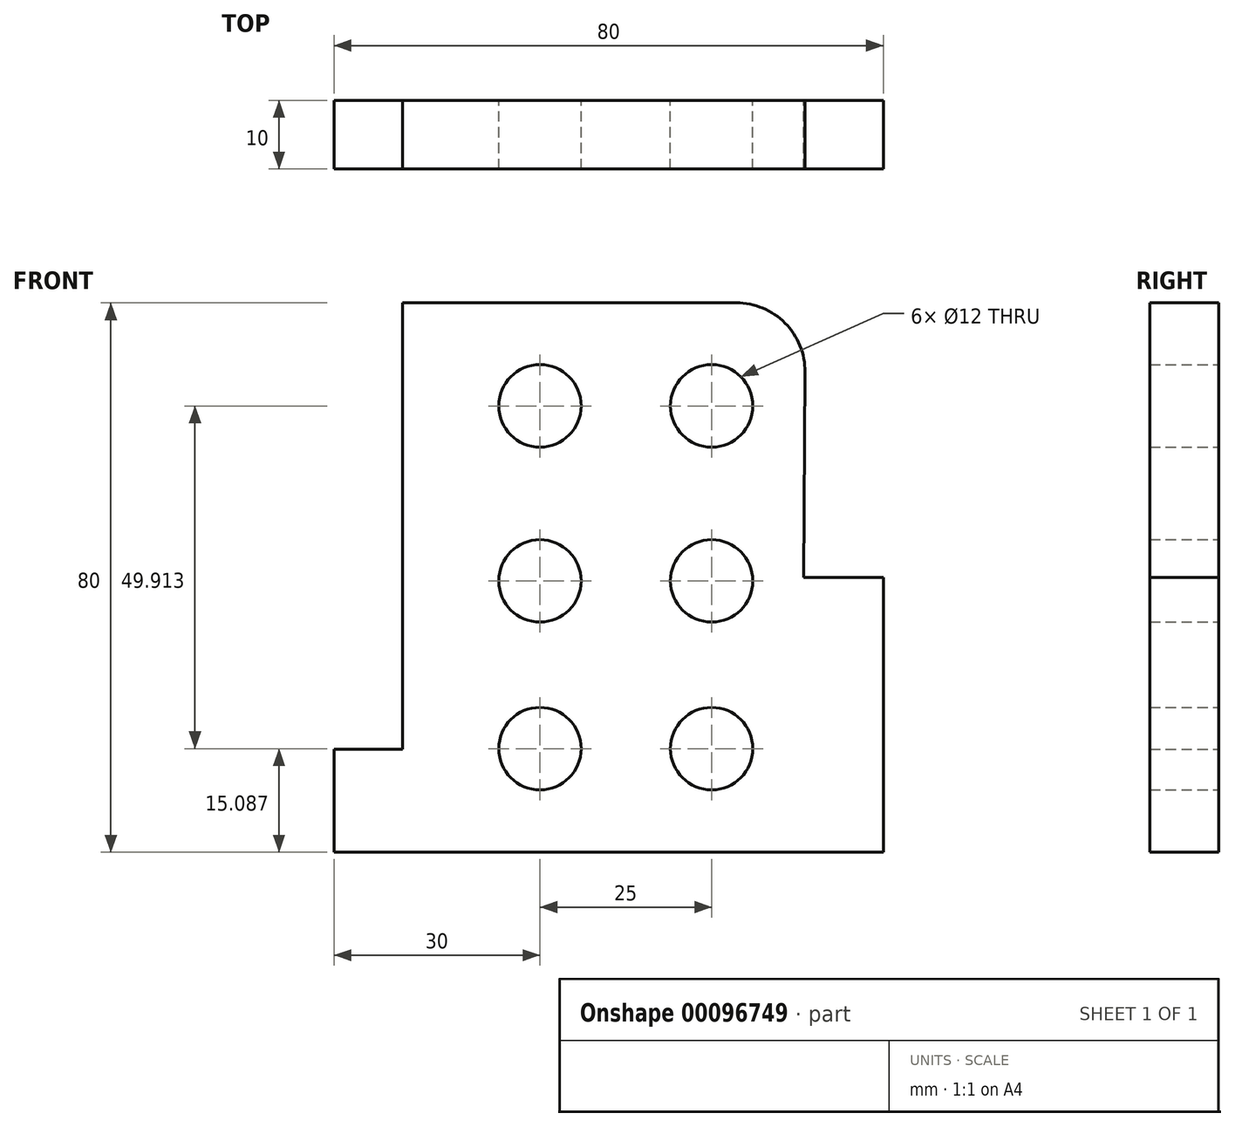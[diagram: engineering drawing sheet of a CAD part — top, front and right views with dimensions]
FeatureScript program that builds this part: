
annotation { "Feature Type Name" : "Feature", "Feature Type Description" : "" }
export const myFeature = defineFeature(function(context is Context, id is Id, definition is map)
    precondition{}
    {
        {
            var Q0;
            Q0=qCreatedBy(makeId("Front.planeOp"),FACE);
            var sketch = newSketch(context, id + "F0", { "sketchPlane" : qUnion([Q0])});
            skLineSegment(sketch, "E0", {"start": v(0, 0) * mm, "end": v(80, 0) * mm});
            skLineSegment(sketch, "E1", {"start": v(80, 0) * mm, "end": v(80, 40) * mm});
            skLineSegment(sketch, "E2", {"start": v(0, 0) * mm, "end": v(0, 15) * mm});
            skLineSegment(sketch, "E3", {"start": v(0, 15) * mm, "end": v(10, 15) * mm});
            skLineSegment(sketch, "E4", {"start": v(10, 15) * mm, "end": v(10, 80) * mm});
            skLineSegment(sketch, "E5", {"start": v(80, 40) * mm, "end": v(68.4, 40) * mm});
            skLineSegment(sketch, "E6", {"start": v(10, 80) * mm, "end": v(58.6, 80) * mm});
            skLineSegment(sketch, "E7", {"start": v(68.6, 69.93) * mm, "end": v(68.4, 40) * mm});
            skPoint(sketch, "E8.visualSharp", {"position": v(68.68, 80) * mm});
            skArc(sketch, "E8.filletArc", {"start": v(68.6, 69.93) * mm, "mid": v(65.7, 77.05) * mm, "end": v(58.6, 80) * mm});
            skCircle(sketch, "E9", {"center": v(30, 15.09) * mm, "radius": 6 * mm});
            skCircle(sketch, "E10", {"center": v(30, 39.51) * mm, "radius": 6 * mm});
            skCircle(sketch, "E11", {"center": v(30, 65) * mm, "radius": 6 * mm});
            skCircle(sketch, "E12", {"center": v(55, 15.09) * mm, "radius": 6 * mm});
            skCircle(sketch, "E13", {"center": v(55, 39.51) * mm, "radius": 6 * mm});
            skCircle(sketch, "E14", {"center": v(55, 65) * mm, "radius": 6 * mm});
            skSolve(sketch);
        }
        {
            var Q0;
            Q0 = qSketchRegion(id + "F0", true);
            extrude(context, id + "F1", {"entities" : qUnion([Q0]), "depth" : 10 * mm});
        }
    });
